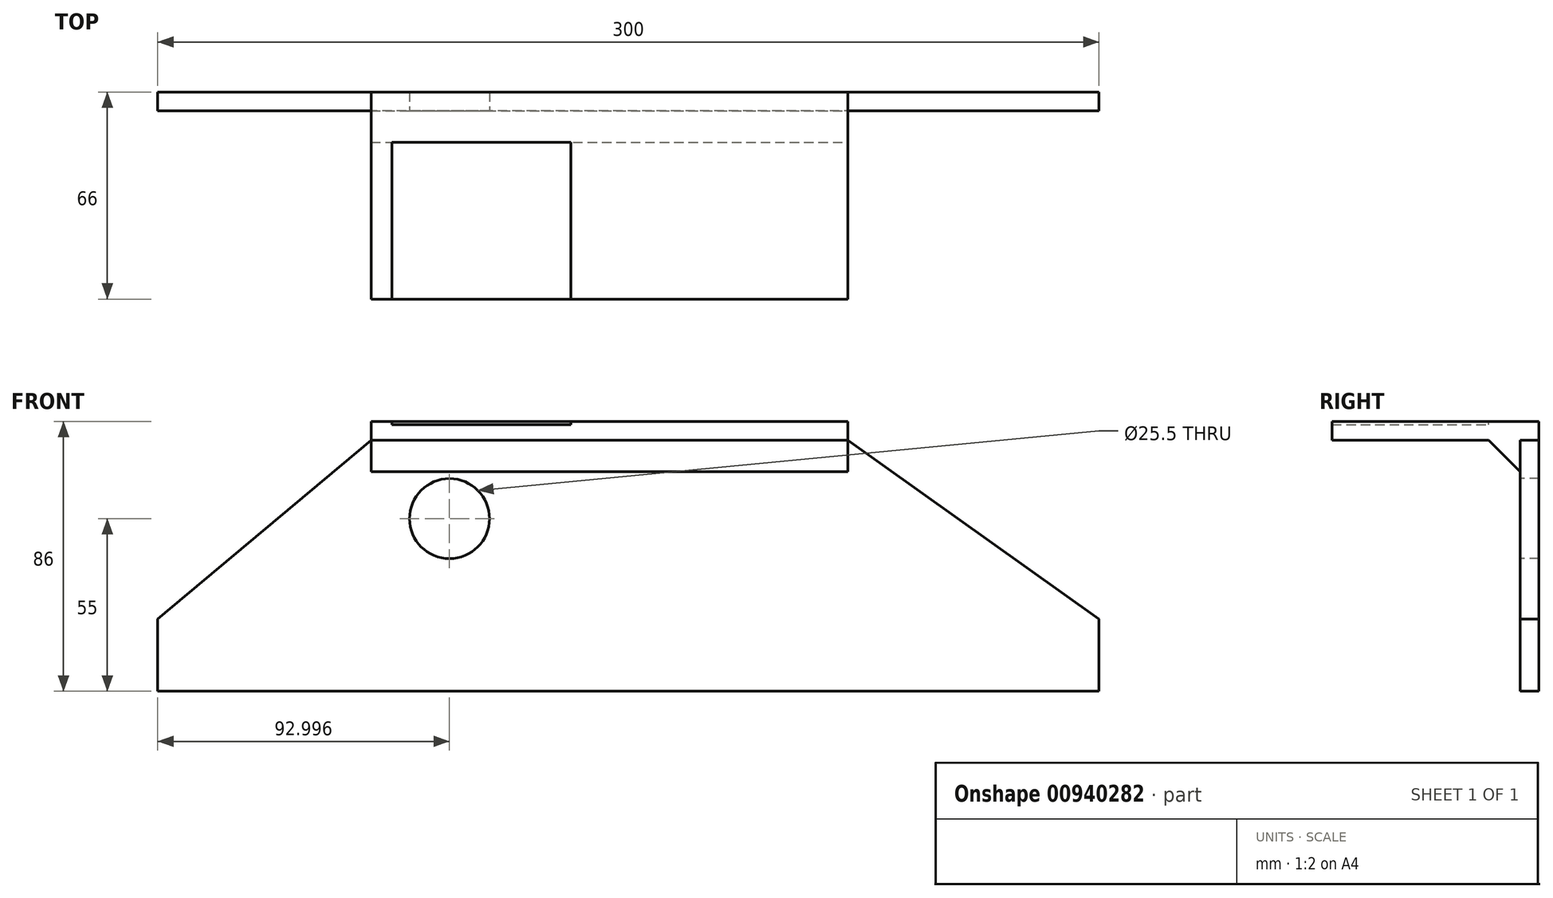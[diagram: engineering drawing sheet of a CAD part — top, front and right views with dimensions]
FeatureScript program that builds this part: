
annotation { "Feature Type Name" : "Feature", "Feature Type Description" : "" }
export const myFeature = defineFeature(function(context is Context, id is Id, definition is map)
    precondition{}
    {
        {
            var Q0;
            Q0=qCreatedBy(makeId("Front.planeOp"),FACE);
            var sketch = newSketch(context, id + "F0", { "sketchPlane" : qUnion([Q0])});
            skLineSegment(sketch, "E0", {"start": v(-65.01, 0) * mm, "end": v(-65.01, 23) * mm});
            skLineSegment(sketch, "E1", {"start": v(2.99, 80) * mm, "end": v(2.99, 86) * mm});
            skLineSegment(sketch, "E2", {"start": v(2.99, 86) * mm, "end": v(154.99, 86) * mm});
            skLineSegment(sketch, "E3", {"start": v(154.99, 86) * mm, "end": v(154.99, 80) * mm});
            skLineSegment(sketch, "E4", {"start": v(234.99, 23) * mm, "end": v(234.99, 0) * mm});
            skLineSegment(sketch, "E5", {"start": v(234.99, 0) * mm, "end": v(-65.01, 0) * mm});
            skLineSegment(sketch, "E6", {"start": v(2.99, 80) * mm, "end": v(-65.01, 23) * mm});
            skLineSegment(sketch, "E7", {"start": v(154.99, 80) * mm, "end": v(234.99, 23) * mm});
            skPoint(sketch, "E8.end.orphan", {"position": v(2.99, 23) * mm});
            skPoint(sketch, "E9.start.orphan", {"position": v(154.99, 23) * mm});
            skSolve(sketch);
        }
        {
            var Q0;
            Q0=makeQuery(id+"F0.imprint","IMPRINT",FACE,{"disambiguationData":[TD([[makeQuery(id+"F0.imprint","IMPRINT",EDGE,{"derivedFrom":sQuery(id+"F0.wireOp",EDGE,"E0")}),-1.0]])]});
            extrude(context, id + "F1", {"entities" : qUnion([Q0]), "depth" : 6 * mm, "offsetDistance" : 25 * mm});
        }
        {
            var Q0;
            Q0=makeQuery(id+"F1.opExtrude","CAP_FACE",FACE,{"disambiguationData":[OSD([sQuery(id+"F0.wireOp",EDGE,"E0"),sQuery(id+"F0.wireOp",EDGE,"E1"),sQuery(id+"F0.wireOp",EDGE,"E2"),sQuery(id+"F0.wireOp",EDGE,"E3"),sQuery(id+"F0.wireOp",EDGE,"E4"),sQuery(id+"F0.wireOp",EDGE,"E5"),sQuery(id+"F0.wireOp",EDGE,"E6"),sQuery(id+"F0.wireOp",EDGE,"E7")])],"isStart":false});
            var sketch = newSketch(context, id + "F2", { "sketchPlane" : qUnion([Q0])});
            skLineSegment(sketch, "E10.bottom", {"start": v(2.99, 86) * mm, "end": v(154.99, 86) * mm});
            skLineSegment(sketch, "E10.top", {"start": v(2.99, 80) * mm, "end": v(154.99, 80) * mm});
            skLineSegment(sketch, "E10.left", {"start": v(2.99, 86) * mm, "end": v(2.99, 80) * mm});
            skLineSegment(sketch, "E10.right", {"start": v(154.99, 86) * mm, "end": v(154.99, 80) * mm});
            skSolve(sketch);
        }
        {
            var Q0;
            Q0=makeQuery(id+"F2.imprint","IMPRINT",FACE,{"disambiguationData":[TD([[makeQuery(id+"F2.imprint","IMPRINT",EDGE,{"derivedFrom":sQuery(id+"F2.wireOp",EDGE,"E10.bottom")}),-1.0]])]});
            extrude(context, id + "F3", {"entities" : qUnion([Q0]), "operationType" : NewBodyOperationType.ADD, "depth" : 60 * mm, "offsetDistance" : 25 * mm});
        }
        {
            var Q0;
            Q0=makeQuery(id+"F3.boolean.opBoolean","MERGE",FACE,{"derivedFrom":[makeQuery(id+"F1.opExtrude","SWEPT_FACE",FACE,{"disambiguationData":[OSD([sQuery(id+"F0.wireOp",EDGE,"E2")])]}),makeQuery(id+"F3.opExtrude","SWEPT_FACE",FACE,{"disambiguationData":[OSD([sQuery(id+"F2.wireOp",EDGE,"E10.bottom")])]})]});
            var sketch = newSketch(context, id + "F4", { "sketchPlane" : qUnion([Q0])});
            skPoint(sketch, "E11.bottom.start.orphan", {"position": v(78.99, -66) * mm});
            skLineSegment(sketch, "E12.bottom", {"start": v(66.69, -66) * mm, "end": v(9.69, -66) * mm});
            skLineSegment(sketch, "E12.top", {"start": v(66.69, -16) * mm, "end": v(9.69, -16) * mm});
            skLineSegment(sketch, "E12.left", {"start": v(66.69, -66) * mm, "end": v(66.69, -16) * mm});
            skLineSegment(sketch, "E12.right", {"start": v(9.69, -66) * mm, "end": v(9.69, -16) * mm});
            skSolve(sketch);
        }
        {
            var Q0;
            Q0=makeQuery(id+"F4.imprint","IMPRINT",FACE,{"disambiguationData":[TD([[makeQuery(id+"F4.imprint","IMPRINT",EDGE,{"derivedFrom":sQuery(id+"F4.wireOp",EDGE,"E12.bottom")}),1.0]])]});
            extrude(context, id + "F5", {"entities" : qUnion([Q0]), "operationType" : NewBodyOperationType.REMOVE, "oppositeDirection" : true, "depth" : 1 * mm, "offsetDistance" : 25 * mm});
        }
        {
            var Q0;
            Q0=makeQuery(id+"F3.opExtrude","SWEPT_FACE",FACE,{"disambiguationData":[OSD([sQuery(id+"F2.wireOp",EDGE,"E10.top")])]});
            var sketch = newSketch(context, id + "F6", { "sketchPlane" : qUnion([Q0])});
            skLineSegment(sketch, "E13.bottom", {"start": v(2.99, 16) * mm, "end": v(154.99, 16) * mm});
            skLineSegment(sketch, "E13.top", {"start": v(2.99, 6) * mm, "end": v(154.99, 6) * mm});
            skLineSegment(sketch, "E13.left", {"start": v(2.99, 16) * mm, "end": v(2.99, 6) * mm});
            skLineSegment(sketch, "E13.right", {"start": v(154.99, 16) * mm, "end": v(154.99, 6) * mm});
            skSolve(sketch);
        }
        {
            var Q0;
            Q0=makeQuery(id+"F6.imprint","IMPRINT",FACE,{"disambiguationData":[TD([[makeQuery(id+"F6.imprint","IMPRINT",EDGE,{"derivedFrom":sQuery(id+"F6.wireOp",EDGE,"E13.bottom")}),-1.0]])]});
            extrude(context, id + "F7", {"entities" : qUnion([Q0]), "operationType" : NewBodyOperationType.ADD, "depth" : 10 * mm, "offsetDistance" : 25 * mm});
        }
        {
            var Q0;
            Q0=makeQuery(id+"F7.boolean.opBoolean","MERGE",FACE,{"derivedFrom":[makeQuery(id+"F3.boolean.opBoolean","MERGE",FACE,{"derivedFrom":[makeQuery(id+"F1.opExtrude","SWEPT_FACE",FACE,{"disambiguationData":[OSD([sQuery(id+"F0.wireOp",EDGE,"E1")])]}),makeQuery(id+"F3.opExtrude","SWEPT_FACE",FACE,{"disambiguationData":[OSD([sQuery(id+"F2.wireOp",EDGE,"E10.left")])]})]}),makeQuery(id+"F7.opExtrude","SWEPT_FACE",FACE,{"disambiguationData":[OSD([sQuery(id+"F6.wireOp",EDGE,"E13.left")])]})]});
            var sketch = newSketch(context, id + "F8", { "sketchPlane" : qUnion([Q0])});
            skLineSegment(sketch, "E14", {"start": v(16, 80) * mm, "end": v(6, 70) * mm});
            skLineSegment(sketch, "E15", {"start": v(6, 70) * mm, "end": v(16, 70) * mm});
            skLineSegment(sketch, "E16", {"start": v(16, 70) * mm, "end": v(16, 80) * mm});
            skSolve(sketch);
        }
        {
            var Q0;
            Q0=makeQuery(id+"F8.imprint","IMPRINT",FACE,{"disambiguationData":[TD([[makeQuery(id+"F8.imprint","IMPRINT",EDGE,{"derivedFrom":sQuery(id+"F8.wireOp",EDGE,"E14")}),1.0]])]});
            extrude(context, id + "F9", {"entities" : qUnion([Q0]), "operationType" : NewBodyOperationType.REMOVE, "oppositeDirection" : true, "depth" : 160 * mm, "offsetDistance" : 25 * mm});
        }
        {
            var Q0;
            Q0=makeQuery(id+"F1.opExtrude","CAP_FACE",FACE,{"disambiguationData":[OSD([sQuery(id+"F0.wireOp",EDGE,"E0"),sQuery(id+"F0.wireOp",EDGE,"E1"),sQuery(id+"F0.wireOp",EDGE,"E2"),sQuery(id+"F0.wireOp",EDGE,"E3"),sQuery(id+"F0.wireOp",EDGE,"E4"),sQuery(id+"F0.wireOp",EDGE,"E5"),sQuery(id+"F0.wireOp",EDGE,"E6"),sQuery(id+"F0.wireOp",EDGE,"E7")])],"isStart":false});
            var sketch = newSketch(context, id + "F10", { "sketchPlane" : qUnion([Q0])});
            skCircle(sketch, "E17", {"center": v(27.99, 55) * mm, "radius": 12.75 * mm});
            skSolve(sketch);
        }
        {
            var Q0;
            Q0=makeQuery(id+"F10.imprint","IMPRINT",FACE,{"disambiguationData":[TD([[makeQuery(id+"F10.imprint","IMPRINT",EDGE,{"derivedFrom":sQuery(id+"F10.wireOp",EDGE,"E17")}),1.0]])]});
            extrude(context, id + "F11", {"entities" : qUnion([Q0]), "operationType" : NewBodyOperationType.REMOVE, "oppositeDirection" : true, "depth" : 25 * mm, "offsetDistance" : 25 * mm});
        }
    });
